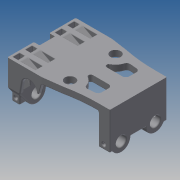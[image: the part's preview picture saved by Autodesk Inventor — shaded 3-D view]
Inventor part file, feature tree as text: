
AUTODESK INVENTOR PART (.ipt)
format: ipt  version: 2014 (Build 180170000, 170)  size: 2,024,448 bytes
history: native  units: in
note: dims shown in document units (in); Inventor stores cm internally (conversion verified against a paired STEP export)
features: fillet x27, extrude x18, sketch x18, mirror x5, plane x2
ambient origin geometry x8: Origin, YZ Plane, XZ Plane, XY Plane, X Axis, Y Axis, Z Axis, Center Point
bodies: Solid1 (feature_tree)
feature tree (70):
  extrude  "Extrusion1"  Depth=1.0441in
  extrude  "Extrusion11"  Depth=0.3543in
  extrude  "Extrusion12"  Depth=2.3622in
  extrude  "Extrusion13"  Depth=0.9843in
  mirror  "Mirror1"
  extrude  "Extrusion14"  Depth=0.2362in
  extrude  "Extrusion4"  Depth=0.6299in
  extrude  "Extrusion15"  Depth=0.1181in
  extrude  "Extrusion16"  Depth=0.3937in
  extrude  "Extrusion17"  Depth=1.5748in
  mirror  "Mirror3"
  extrude  "Extrusion25"  Depth=0.3937in
  extrude  "Extrusion22"  Depth=0.0591in
  plane  "Work Plane1"
  extrude  "Extrusion24"  Depth=0.1181in TaperAngle=0.0deg
  mirror  "Mirror2"
  extrude  "Extrusion26"  Depth=0.1575in TaperAngle=0.0deg
  mirror  "Mirror4"
  fillet  "Fillet23"  Radius=0.9055in
  sketch  "Sketch27"  dims[d84=5.9055in d85=0.0in d87=0.3937in]
  plane  "Work Plane2"
  extrude  "Extrusion28"  Depth=0.3937in
  extrude  "Extrusion29"  Depth=0.7874in
  extrude  "Extrusion27"  Depth=0.1969in TaperAngle=0.0deg
  extrude  "Extrusion30"  Depth=0.1969in
  extrude  "Extrusion31"  Depth=0.2362in TaperAngle=0.0deg
  mirror  "Mirror5"
  fillet  "Fillet8"  Radius=0.315in
  fillet  "Fillet9"  Radius=0.1969in
  fillet  "Fillet10"  Radius=0.1181in
  fillet  "Fillet11"  Radius=0.2362in
  fillet  "Fillet13"  Radius=0.1181in
  fillet  "Fillet14"  Radius=0.0787in
  fillet  "Fillet15"  Radius=0.0984in
  fillet  "Fillet16"  Radius=0.0394in
  fillet  "Fillet17"  Radius=0.0394in
  fillet  "Fillet18"  Radius=0.0197in
  fillet  "Fillet19"  Radius=0.0197in
  fillet  "Fillet22"  Radius=0.0197in
  fillet  "Fillet24"  Radius=0.0197in
  fillet  "Fillet25"  Radius=0.0197in
  fillet  "Fillet26"  Radius=0.0197in
  fillet  "Fillet27"  Radius=0.0197in
  fillet  "Fillet28"  Radius=0.0197in
  fillet  "Fillet29"  Radius=0.0295in
  fillet  "Fillet30"  Radius=0.2362in
  fillet  "Fillet31"  Radius=0.3346in
  fillet  "Fillet32"  Radius=0.1575in
  fillet  "Fillet33"  Radius=1.1811in
  fillet  "Fillet34"  Radius=5.9055in
  fillet  "Fillet35"  Radius=0.0787in
  fillet  "Fillet36"  Radius=0.2756in
  fillet  "Fillet37"  Radius=0.2756in
  sketch  "Sketch1"  dims[d0=1.1713in d1=1.0441in]
  sketch  "Sketch2"  dims[d2=1.5748in d3=0.3543in]
  sketch  "Sketch3"  dims[d4=0.6299in d5=2.3622in]
  sketch  "Sketch4"  dims[d6=0.5906in d7=0.9843in]
  sketch  "Sketch5"  dims[d9=0.2362in d10=0.0in d11=0.2362in]
  sketch  "Sketch11"  dims[d12=1.5748in d13=0.6299in]
  sketch  "Sketch13"  dims[d15=0.3346in d16=0.1181in]
  sketch  "Sketch14"  dims[d26=2.5123in d27=0.0in d66=0.3937in]
  sketch  "Sketch19"  dims[d67=1.9685in d68=1.5748in]
  sketch  "Sketch21"  dims[d69=2.3622in d70=0.0in d71=0.3937in]
  sketch  "Sketch22"  dims[d72=1.9685in d73=0.0in d74=0.0591in]
  sketch  "Sketch23"  dims[d75=0.315in d76=0.1181in d77=0.0in]
  sketch  "Sketch26"  dims[d78=0.0394in d79=0.1575in d80=0.0in d81=0.9055in]
  sketch  "Sketch28"  dims[d88=0.5906in d89=0.7874in]
  sketch  "Sketch29"  dims[d90=0.1575in d91=0.0in d93=0.1969in d94=0.0in]
  sketch  "Sketch30"  dims[d111=0.1181in d112=0.1969in]
  sketch  "Sketch31"  dims[d113=0.1181in d114=0.2362in d115=0.0in d117=0.315in d119=0.1969in d123=0.1181in d124=0.2362in d125=0.0in d126=0.1181in d127=0.0787in d128=0.0984in d129=0.0394in d130=0.0394in d131=0.0197in d133=0.0197in d134=0.0197in d135=0.0197in d136=0.0197in d137=0.0197in d138=0.0197in d139=0.0197in d142=0.0295in d143=0.2362in d144=0.3346in d145=0.1575in d146=1.1811in d150=5.9055in d151=0.0in d159=0.0787in d160=0.2756in d162=0.2756in d164=0.1575in d165=5.9055in d166=0.0in d167=0.1181in d168=0.2756in d169=0.0787in d175=0.0in d176=0.2165in d177=0.0945in d178=0.2165in d179=0.7874in d180=0.0in d181=0.315in d182=0.1969in d183=0.7874in d184=0.0in d187=0.3543in d188=0.3937in d189=0.7874in d190=0.0in d191=0.0787in d192=0.0in d193=0.0787in d194=0.0in d195=0.0394in d196=0.0394in d197=0.0394in d198=0.0394in d199=0.0394in d200=0.0394in d201=0.0197in d202=0.0197in d203=0.0197in d204=0.0197in d205=0.0394in d206=0.0394in d207=0.0098in d208=0.0098in]
